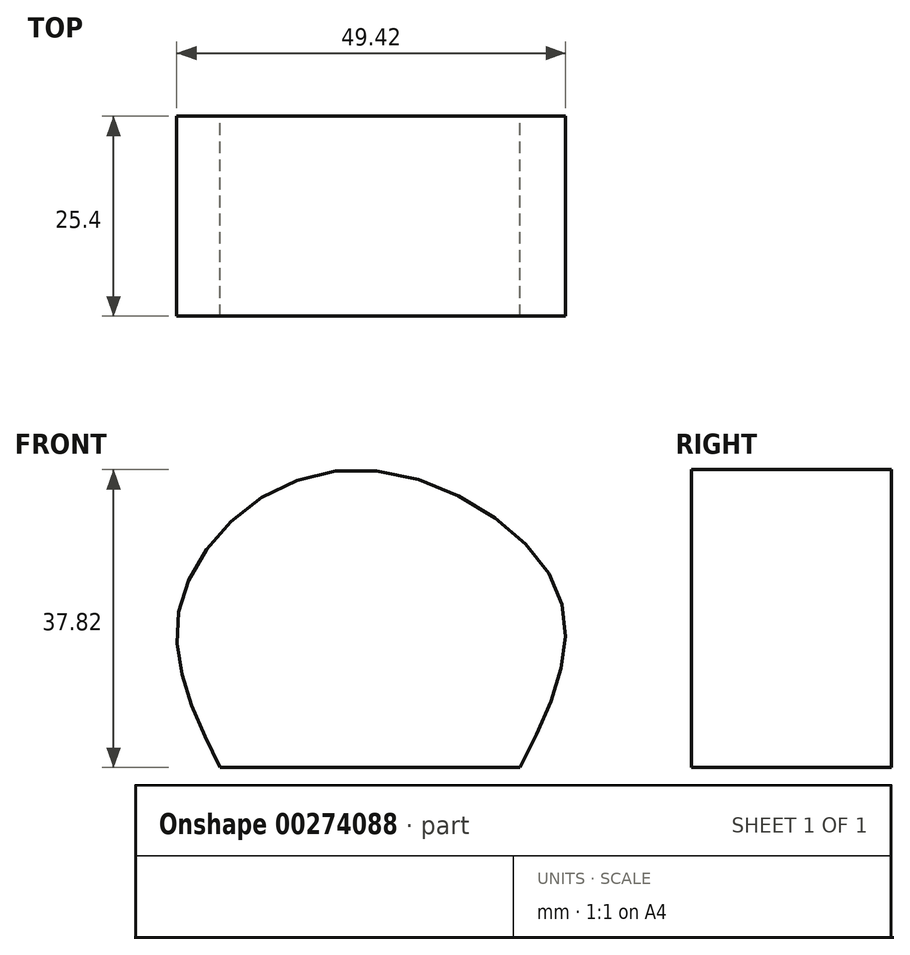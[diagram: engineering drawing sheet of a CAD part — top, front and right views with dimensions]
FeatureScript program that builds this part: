
annotation { "Feature Type Name" : "Feature", "Feature Type Description" : "" }
export const myFeature = defineFeature(function(context is Context, id is Id, definition is map)
    precondition{}
    {
        {
            var Q0;
            Q0=qCreatedBy(makeId("Front.planeOp"),FACE);
            var sketch = newSketch(context, id + "F0", { "sketchPlane" : qUnion([Q0])});
            skLineSegment(sketch, "E0", {"start": v(-21.53, -5.46) * mm, "end": v(16.57, -5.46) * mm});
            skFitSpline(sketch, "E1", {"points": [v(-21.53, -5.46) * mm, v(-26.54, 15.42) * mm, v(-6.08, 32.29) * mm, v(21.3, 17.08) * mm, v(16.57, -5.46) * mm], "startDerivative": vector(-44.42, 90.01) * mm, "endDerivative": vector(-48.91, -96.8) * mm});
            skSolve(sketch);
        }
        {
            var Q0;
            Q0=makeQuery(id+"F0.imprint","IMPRINT",FACE,{"disambiguationData":[TD([[makeQuery(id+"F0.imprint","IMPRINT",EDGE,{"derivedFrom":sQuery(id+"F0.wireOp",EDGE,"E0")}),1.0]])]});
            extrude(context, id + "F1", {"entities" : qUnion([Q0]), "depth" : 25.4 * mm});
        }
    });
